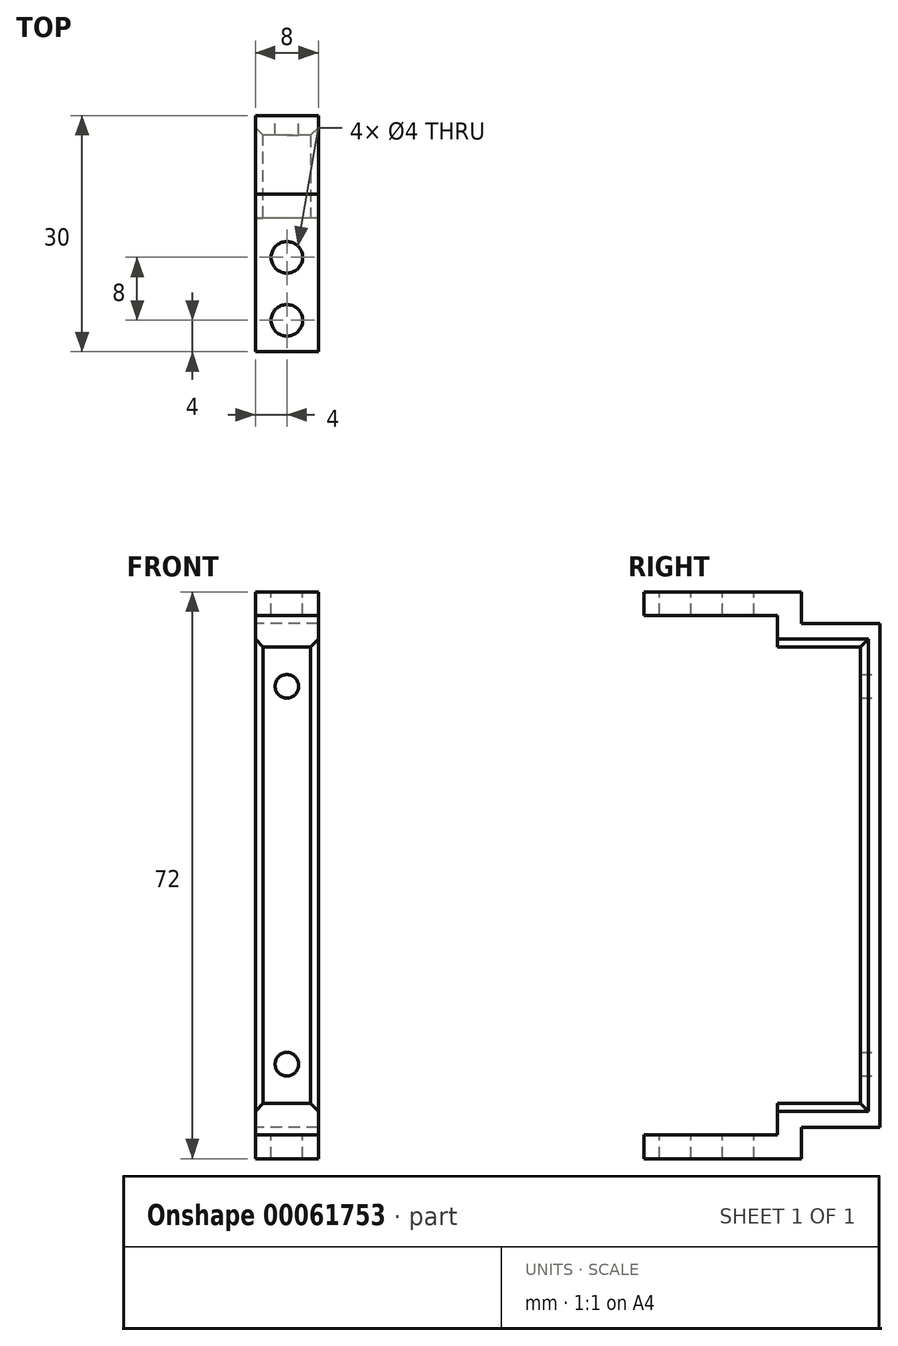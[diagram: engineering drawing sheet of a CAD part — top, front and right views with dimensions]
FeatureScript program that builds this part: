
annotation { "Feature Type Name" : "Feature", "Feature Type Description" : "" }
export const myFeature = defineFeature(function(context is Context, id is Id, definition is map)
    precondition{}
    {
        {
            var Q0;
            Q0=qCreatedBy(makeId("Right.planeOp"),FACE);
            var sketch = newSketch(context, id + "F0", { "sketchPlane" : qUnion([Q0])});
            skLineSegment(sketch, "E0", {"start": v(4, 36) * mm, "end": v(24, 36) * mm});
            skLineSegment(sketch, "E1", {"start": v(34, 32) * mm, "end": v(34, -15.69) * mm});
            skLineSegment(sketch, "E2.1", {"start": v(4, 33) * mm, "end": v(21, 33) * mm});
            skLineSegment(sketch, "E3", {"start": v(4, 36) * mm, "end": v(4, 33) * mm});
            skLineSegment(sketch, "E4", {"start": v(26, 0) * mm, "end": v(-14.36, 0) * mm, "construction": true});
            skLineSegment(sketch, "E5", {"start": v(4, -33) * mm, "end": v(21, -33) * mm});
            skLineSegment(sketch, "E6", {"start": v(24, -36) * mm, "end": v(4, -36) * mm});
            skLineSegment(sketch, "E7", {"start": v(4, -36) * mm, "end": v(4, -33) * mm});
            skLineSegment(sketch, "E8", {"start": v(31.5, -29) * mm, "end": v(31.5, 29) * mm});
            skLineSegment(sketch, "E9", {"start": v(21, -33) * mm, "end": v(21, -29) * mm});
            skLineSegment(sketch, "E10", {"start": v(21, -29) * mm, "end": v(31.5, -29) * mm});
            skLineSegment(sketch, "E11", {"start": v(34, -15.69) * mm, "end": v(34, -32) * mm});
            skLineSegment(sketch, "E12", {"start": v(34, -32) * mm, "end": v(24, -32) * mm});
            skLineSegment(sketch, "E13", {"start": v(24, -32) * mm, "end": v(24, -36) * mm});
            skLineSegment(sketch, "E14", {"start": v(31.5, 29) * mm, "end": v(21, 29) * mm});
            skLineSegment(sketch, "E15", {"start": v(21, 29) * mm, "end": v(21, 33) * mm});
            skLineSegment(sketch, "E16", {"start": v(24, 36) * mm, "end": v(24, 32) * mm});
            skLineSegment(sketch, "E17", {"start": v(24, 32) * mm, "end": v(34, 32) * mm});
            skSolve(sketch);
        }
        {
            var Q0;
            Q0=makeQuery(id+"F0.imprint","IMPRINT",FACE,{"disambiguationData":[TD([[makeQuery(id+"F0.imprint","IMPRINT",EDGE,{"derivedFrom":sQuery(id+"F0.wireOp",EDGE,"E0")}),-1.0]])]});
            extrude(context, id + "F1", {"entities" : qUnion([Q0]), "depth" : 8 * mm});
        }
        {
            var Q0;
            Q0=makeQuery(id+"F1.opExtrude","SWEPT_FACE",FACE,{"disambiguationData":[OSD([sQuery(id+"F0.wireOp",EDGE,"E0")])]});
            var sketch = newSketch(context, id + "F2", { "sketchPlane" : qUnion([Q0])});
            skLineSegment(sketch, "E18.bottom", {"start": v(0, 4) * mm, "end": v(6.02, 4) * mm});
            skLineSegment(sketch, "E18.top", {"start": v(0, -1) * mm, "end": v(6.02, -1) * mm});
            skLineSegment(sketch, "E18.left", {"start": v(0, 4) * mm, "end": v(0, -1) * mm});
            skLineSegment(sketch, "E18.right", {"start": v(6.02, 4) * mm, "end": v(6.02, -1) * mm});
            skSolve(sketch);
        }
        {
            var Q0;
            Q0=makeQuery(id+"F2.imprint","IMPRINT",FACE,{"disambiguationData":[TD([[makeQuery(id+"F2.imprint","IMPRINT",EDGE,{"derivedFrom":sQuery(id+"F2.wireOp",EDGE,"E18.bottom")}),1.0]])]});
            extrude(context, id + "F3", {"entities" : qUnion([Q0]), "operationType" : NewBodyOperationType.REMOVE, "oppositeDirection" : true, "depth" : 72 * mm});
        }
        {
            var Q0;
            Q0=makeQuery(id+"F1.opExtrude","SWEPT_FACE",FACE,{"disambiguationData":[OSD([sQuery(id+"F0.wireOp",EDGE,"E1")])]});
            var sketch = newSketch(context, id + "F4", { "sketchPlane" : qUnion([Q0])});
            skCircle(sketch, "E19", {"center": v(-4, 24) * mm, "radius": 1.5 * mm});
            skCircle(sketch, "E20", {"center": v(-4, -24) * mm, "radius": 1.5 * mm});
            skLineSegment(sketch, "E21", {"start": v(-4, 24) * mm, "end": v(-4, -24) * mm, "construction": true});
            skPoint(sketch, "E22", {"position": v(-4, 37.5) * mm});
            skLineSegment(sketch, "E23", {"start": v(-4, 24) * mm, "end": v(-4, 37.5) * mm, "construction": true});
            skSolve(sketch);
        }
        {
            var Q0;
            Q0=makeQuery(id+"F4.imprint","IMPRINT",FACE,{"disambiguationData":[TD([[makeQuery(id+"F4.imprint","IMPRINT",EDGE,{"derivedFrom":sQuery(id+"F4.wireOp",EDGE,"E19")}),1.0]])]});
            var Q1;
            Q1=makeQuery(id+"F4.imprint","IMPRINT",FACE,{"disambiguationData":[TD([[makeQuery(id+"F4.imprint","IMPRINT",EDGE,{"derivedFrom":sQuery(id+"F4.wireOp",EDGE,"E20")}),1.0]])]});
            extrude(context, id + "F5", {"entities" : qUnion([Q0, Q1]), "operationType" : NewBodyOperationType.REMOVE, "oppositeDirection" : true, "depth" : 25 * mm});
        }
        {
            var Q0;
            Q0=makeQuery(id+"F1.opExtrude","SWEPT_FACE",FACE,{"disambiguationData":[OSD([sQuery(id+"F0.wireOp",EDGE,"E0")])]});
            var sketch = newSketch(context, id + "F6", { "sketchPlane" : qUnion([Q0])});
            skCircle(sketch, "E24", {"center": v(4, 16) * mm, "radius": 2 * mm});
            skCircle(sketch, "E25", {"center": v(4, 8) * mm, "radius": 2 * mm});
            skSolve(sketch);
        }
        {
            var Q0;
            Q0=makeQuery(id+"F6.imprint","IMPRINT",FACE,{"disambiguationData":[TD([[makeQuery(id+"F6.imprint","IMPRINT",EDGE,{"derivedFrom":sQuery(id+"F6.wireOp",EDGE,"E24")}),1.0]])]});
            var Q1;
            Q1=makeQuery(id+"F6.imprint","IMPRINT",FACE,{"disambiguationData":[TD([[makeQuery(id+"F6.imprint","IMPRINT",EDGE,{"derivedFrom":sQuery(id+"F6.wireOp",EDGE,"E25")}),1.0]])]});
            extrude(context, id + "F7", {"entities" : qUnion([Q0, Q1]), "operationType" : NewBodyOperationType.REMOVE, "oppositeDirection" : true, "depth" : 72 * mm});
        }
        {
            var Q0;
            Q0=makeQuery(id+"F1.opExtrude","CAP_EDGE",EDGE,{"disambiguationData":[OSD([sQuery(id+"F0.wireOp",EDGE,"E8")])],"isStart":false});
            var Q1;
            Q1=makeQuery(id+"F1.opExtrude","CAP_EDGE",EDGE,{"disambiguationData":[OSD([sQuery(id+"F0.wireOp",EDGE,"E8")])],"isStart":true});
            var Q2;
            Q2=makeQuery(id+"F1.opExtrude","CAP_EDGE",EDGE,{"disambiguationData":[OSD([sQuery(id+"F0.wireOp",EDGE,"E14")])],"isStart":false});
            var Q3;
            Q3=makeQuery(id+"F1.opExtrude","CAP_EDGE",EDGE,{"disambiguationData":[OSD([sQuery(id+"F0.wireOp",EDGE,"E14")])],"isStart":true});
            var Q4;
            Q4=makeQuery(id+"F1.opExtrude","CAP_EDGE",EDGE,{"disambiguationData":[OSD([sQuery(id+"F0.wireOp",EDGE,"E10")])],"isStart":false});
            var Q5;
            Q5=makeQuery(id+"F1.opExtrude","CAP_EDGE",EDGE,{"disambiguationData":[OSD([sQuery(id+"F0.wireOp",EDGE,"E10")])],"isStart":true});
            chamfer(context, id + "F8", {"entities" : qUnion([Q0, Q1, Q2, Q3, Q4, Q5]), "width" : 1 * mm, "tangentPropagation" : true});
        }
    });
